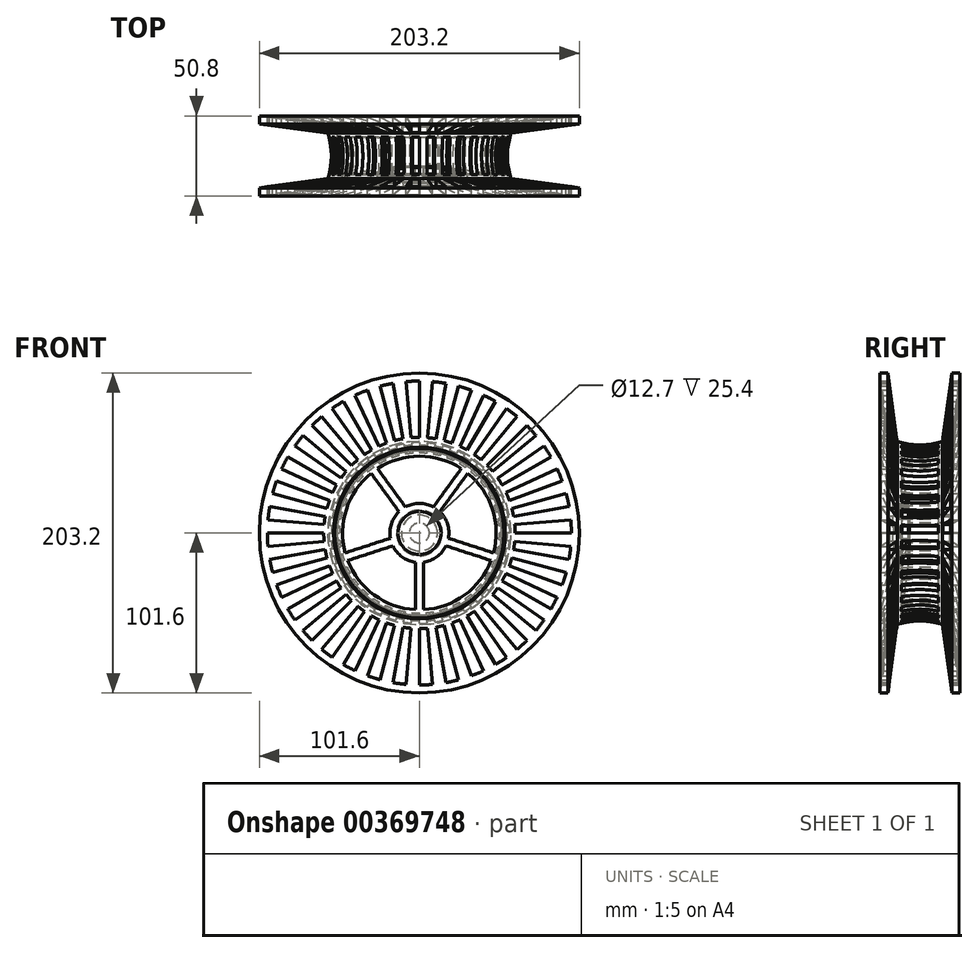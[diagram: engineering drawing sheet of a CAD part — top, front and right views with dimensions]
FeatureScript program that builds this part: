
annotation { "Feature Type Name" : "Feature", "Feature Type Description" : "" }
export const myFeature = defineFeature(function(context is Context, id is Id, definition is map)
    precondition{}
    {
        {
            var Q0;
            Q0=qCreatedBy(makeId("Top.planeOp"),FACE);
            var sketch = newSketch(context, id + "F0", { "sketchPlane" : qUnion([Q0])});
            skLineSegment(sketch, "E0", {"start": v(0, -32.06) * mm, "end": v(0, 32.06) * mm, "construction": true});
            skSolve(sketch);
        }
        {
            var Q0;
            Q0=qCreatedBy(makeId("Right.planeOp"),FACE);
            var sketch = newSketch(context, id + "F1", { "sketchPlane" : qUnion([Q0])});
            skArc(sketch, "E1", {"start": v(-19.05, 54.5) * mm, "mid": v(0, 50.8) * mm, "end": v(19.05, 54.5) * mm});
            skLineSegment(sketch, "E2", {"start": v(0, 0) * mm, "end": v(0, 101.6) * mm, "construction": true});
            skLineSegment(sketch, "E3", {"start": v(-25.4, 101.6) * mm, "end": v(25.4, 101.6) * mm});
            skLineSegment(sketch, "E4", {"start": v(-25.4, 101.6) * mm, "end": v(-19.05, 54.5) * mm});
            skLineSegment(sketch, "E5", {"start": v(25.4, 101.6) * mm, "end": v(19.05, 54.5) * mm});
            skPoint(sketch, "E6.visualSharp", {"position": v(25.4, 101.6) * mm});
            skPoint(sketch, "E7.visualSharp", {"position": v(-25.4, 101.6) * mm});
            skPoint(sketch, "E8.visualSharp", {"position": v(-19.05, 54.5) * mm});
            skPoint(sketch, "E9.visualSharp", {"position": v(19.05, 54.5) * mm});
            skSolve(sketch);
        }
        {
            var Q0;
            Q0=qSketchRegion(id+"F1",true);
            var Q1;
            Q1=sQuery(id+"F0.wireOp",EDGE,"E0");
            revolve(context, id + "F2", {"entities" : qUnion([Q0]), "axis" : qUnion([Q1]), "revolveType" : RevolveType.FULL});
        }
        {
            var Q0;
            Q0=qCreatedBy(makeId("Right.planeOp"),FACE);
            var sketch = newSketch(context, id + "F3", { "sketchPlane" : qUnion([Q0])});
            skLineSegment(sketch, "E10.0", {"start": v(21.12, 107.87) * mm, "end": v(14.42, 58.21) * mm});
            skArc(sketch, "E10.1", {"start": v(-14.42, 58.21) * mm, "mid": v(0, 55.88) * mm, "end": v(14.42, 58.21) * mm});
            skLineSegment(sketch, "E10.2", {"start": v(-21.12, 107.87) * mm, "end": v(-14.42, 58.21) * mm});
            skLineSegment(sketch, "E11", {"start": v(-21.12, 107.87) * mm, "end": v(21.12, 107.87) * mm});
            skSolve(sketch);
        }
        {
            var Q0;
            Q0=qSketchRegion(id+"F3",true);
            var Q1;
            Q1=sQuery(id+"F0.wireOp",EDGE,"E0");
            revolve(context, id + "F4", {"operationType" : NewBodyOperationType.REMOVE, "entities" : qUnion([Q0]), "axis" : qUnion([Q1]), "revolveType" : RevolveType.FULL, "oppositeDirection" : true});
        }
        {
            var Q0;
            Q0=sQuery(id+"F0.wireOp",EDGE,"E0");
            cPlane(context, id + "F5", {"entities" : qUnion([Q0]), "cplaneType" : CPlaneType.LINE_ANGLE, "offset" : 152.4 * mm, "angle" : 95 * degree, "width" : 152.4 * mm, "height" : 152.4 * mm});
        }
        {
            var Q0;
            Q0=qCreatedBy(id+"F5.planeOp",FACE);
            var sketch = newSketch(context, id + "F6", { "sketchPlane" : qUnion([Q0])});
            skLineSegment(sketch, "E12", {"start": v(-31.7, 96.52) * mm, "end": v(31.7, 96.52) * mm});
            skLineSegment(sketch, "E13", {"start": v(20.27, 101.6) * mm, "end": v(25.4, 101.6) * mm, "construction": true});
            skArc(sketch, "E14", {"start": v(-14.42, 58.21) * mm, "mid": v(0, 55.88) * mm, "end": v(14.42, 58.21) * mm, "construction": true});
            skLineSegment(sketch, "E15", {"start": v(-14.42, 60.75) * mm, "end": v(-31.7, 60.75) * mm});
            skLineSegment(sketch, "E16", {"start": v(-31.7, 60.75) * mm, "end": v(-31.7, 96.52) * mm});
            skLineSegment(sketch, "E17", {"start": v(-11.88, 58.21) * mm, "end": v(-11.88, 45.31) * mm});
            skLineSegment(sketch, "E18", {"start": v(-11.88, 45.31) * mm, "end": v(0, 45.31) * mm});
            skArc(sketch, "E19", {"start": v(-11.88, 58.21) * mm, "mid": v(-12.63, 60.01) * mm, "end": v(-14.42, 60.75) * mm});
            skLineSegment(sketch, "E20", {"start": v(0, 0) * mm, "end": v(0, 96.52) * mm, "construction": true});
            skLineSegment(sketch, "E21.0.MirrorCS", {"start": v(31.7, 60.75) * mm, "end": v(31.7, 96.52) * mm});
            skLineSegment(sketch, "E22.0.MirrorCS", {"start": v(14.42, 60.75) * mm, "end": v(31.7, 60.75) * mm});
            skArc(sketch, "E23.0.MirrorCS", {"start": v(11.88, 58.21) * mm, "mid": v(12.63, 60.01) * mm, "end": v(14.42, 60.75) * mm});
            skLineSegment(sketch, "E24.0.MirrorCS", {"start": v(11.88, 58.21) * mm, "end": v(11.88, 45.31) * mm});
            skLineSegment(sketch, "E25.0.MirrorCS", {"start": v(11.88, 45.31) * mm, "end": v(0, 45.31) * mm});
            skSolve(sketch);
        }
        {
            var Q0;
            Q0=qSketchRegion(id+"F6",true);
            var Q1;
            Q1=sQuery(id+"F0.wireOp",EDGE,"E0");
            revolve(context, id + "F7", {"entities" : qUnion([Q0]), "axis" : qUnion([Q1]), "revolveType" : RevolveType.ONE_DIRECTION, "angle" : 5 * degree});
        }
        {
            var Q0;
            Q0=makeQuery(id+"F7.opRevolve","SWEPT_BODY",BODY,{"disambiguationData":[OSD([sQuery(id+"F6.wireOp",EDGE,"E12"),sQuery(id+"F6.wireOp",EDGE,"E15"),sQuery(id+"F6.wireOp",EDGE,"E16"),sQuery(id+"F6.wireOp",EDGE,"E17"),sQuery(id+"F6.wireOp",EDGE,"E18"),sQuery(id+"F6.wireOp",EDGE,"E19"),sQuery(id+"F6.wireOp",EDGE,"E21.0.MirrorCS"),sQuery(id+"F6.wireOp",EDGE,"E22.0.MirrorCS"),sQuery(id+"F6.wireOp",EDGE,"E23.0.MirrorCS"),sQuery(id+"F6.wireOp",EDGE,"E24.0.MirrorCS"),sQuery(id+"F6.wireOp",EDGE,"E25.0.MirrorCS")])]});
            var Q1;
            Q1=sQuery(id+"F0.wireOp",EDGE,"E0");
            circularPattern(context, id + "F8", {"operationType" : NewBodyOperationType.REMOVE, "entities" : qUnion([Q0]), "axis" : qUnion([Q1]), "angle" : 360 * degree, "instanceCount" : 36, "equalSpace" : true, "computeTransformsWithoutBuiltin" : true});
        }
        {
            var Q0;
            Q0=qCreatedBy(makeId("Right.planeOp"),FACE);
            var sketch = newSketch(context, id + "F9", { "sketchPlane" : qUnion([Q0])});
            skArc(sketch, "E26.0", {"start": v(-19.05, 54.5) * mm, "mid": v(0, 50.8) * mm, "end": v(19.05, 54.5) * mm, "construction": true});
            skLineSegment(sketch, "E27.0", {"start": v(-25.4, 101.6) * mm, "end": v(-19.05, 54.5) * mm, "construction": true});
            skLineSegment(sketch, "E28", {"start": v(-6.8, 0) * mm, "end": v(-6.8, 14.54) * mm});
            skLineSegment(sketch, "E29", {"start": v(-11.88, 52.2) * mm, "end": v(-6.8, 14.54) * mm});
            skLineSegment(sketch, "E30", {"start": v(-11.88, 0) * mm, "end": v(-11.88, 13.66) * mm});
            skLineSegment(sketch, "E31", {"start": v(-11.88, 13.66) * mm, "end": v(-17.3, 53.84) * mm});
            skLineSegment(sketch, "E32", {"start": v(-11.88, 0) * mm, "end": v(-6.8, 0) * mm});
            skLineSegment(sketch, "E33", {"start": v(-17.3, 53.84) * mm, "end": v(-11.88, 52.2) * mm});
            skSolve(sketch);
        }
        {
            var Q0;
            Q0=makeQuery(id+"F9.imprint","IMPRINT",FACE,{"disambiguationData":[TD([[makeQuery(id+"F9.imprint","IMPRINT",EDGE,{"derivedFrom":sQuery(id+"F9.wireOp",EDGE,"E28")}),1.0]])]});
            var Q1;
            Q1=sQuery(id+"F0.wireOp",EDGE,"E0");
            revolve(context, id + "F10", {"operationType" : NewBodyOperationType.ADD, "entities" : qUnion([Q0]), "axis" : qUnion([Q1]), "revolveType" : RevolveType.FULL});
        }
        {
            var Q0;
            Q0=qCreatedBy(makeId("Front.planeOp"),FACE);
            var sketch = newSketch(context, id + "F11", { "sketchPlane" : qUnion([Q0])});
            skLineSegment(sketch, "E34", {"start": v(0, 0) * mm, "end": v(14.17, 19.5) * mm, "construction": true});
            skLineSegment(sketch, "E35", {"start": v(0, 0) * mm, "end": v(-14.33, 19.72) * mm, "construction": true});
            skArc(sketch, "E36", {"start": v(26.56, 40.88) * mm, "mid": v(0, 48.76) * mm, "end": v(-26.56, 40.88) * mm});
            skArc(sketch, "E37", {"start": v(8.86, 16.52) * mm, "mid": v(0, 18.74) * mm, "end": v(-8.86, 16.52) * mm});
            skLineSegment(sketch, "E38", {"start": v(-26.56, 40.88) * mm, "end": v(-8.86, 16.52) * mm});
            skLineSegment(sketch, "E39", {"start": v(8.86, 16.52) * mm, "end": v(26.56, 40.88) * mm});
            skPoint(sketch, "E40.orphan", {"position": v(-17.77, 16.69) * mm});
            skPoint(sketch, "E41.orphan", {"position": v(17.77, 16.69) * mm});
            skSolve(sketch);
        }
        {
            var Q0;
            Q0=qSketchRegion(id+"F11",true);
            extrude(context, id + "F12", {"entities" : qUnion([Q0]), "depth" : 59.06 * mm, "symmetric" : true});
        }
        {
            var Q0;
            Q0=makeQuery(id+"F12.opExtrude","SWEPT_BODY",BODY,{"disambiguationData":[OSD([sQuery(id+"F11.wireOp",EDGE,"E36"),sQuery(id+"F11.wireOp",EDGE,"E37"),sQuery(id+"F11.wireOp",EDGE,"E38"),sQuery(id+"F11.wireOp",EDGE,"E39")])]});
            var Q1;
            Q1=sQuery(id+"F0.wireOp",EDGE,"E0");
            circularPattern(context, id + "F13", {"operationType" : NewBodyOperationType.REMOVE, "entities" : qUnion([Q0]), "axis" : qUnion([Q1]), "angle" : 360 * degree, "instanceCount" : 5, "equalSpace" : true, "computeTransformsWithoutBuiltin" : true});
        }
        {
            var Q0;
            Q0=makeQuery(id+"F10.opRevolve","SWEPT_FACE",FACE,{"disambiguationData":[OSD([sQuery(id+"F9.wireOp",EDGE,"E28")])]});
            var sketch = newSketch(context, id + "F14", { "sketchPlane" : qUnion([Q0])});
            skCircle(sketch, "E42", {"center": v(0, 0) * mm, "radius": 11.43 * mm});
            skCircle(sketch, "E43", {"center": v(0, 0) * mm, "radius": 6.35 * mm});
            skSolve(sketch);
        }
        {
            var Q0;
            Q0=qSketchRegion(id+"F14",true);
            extrude(context, id + "F15", {"entities" : qUnion([Q0]), "operationType" : NewBodyOperationType.ADD, "depth" : 25.4 * mm});
        }
    });
